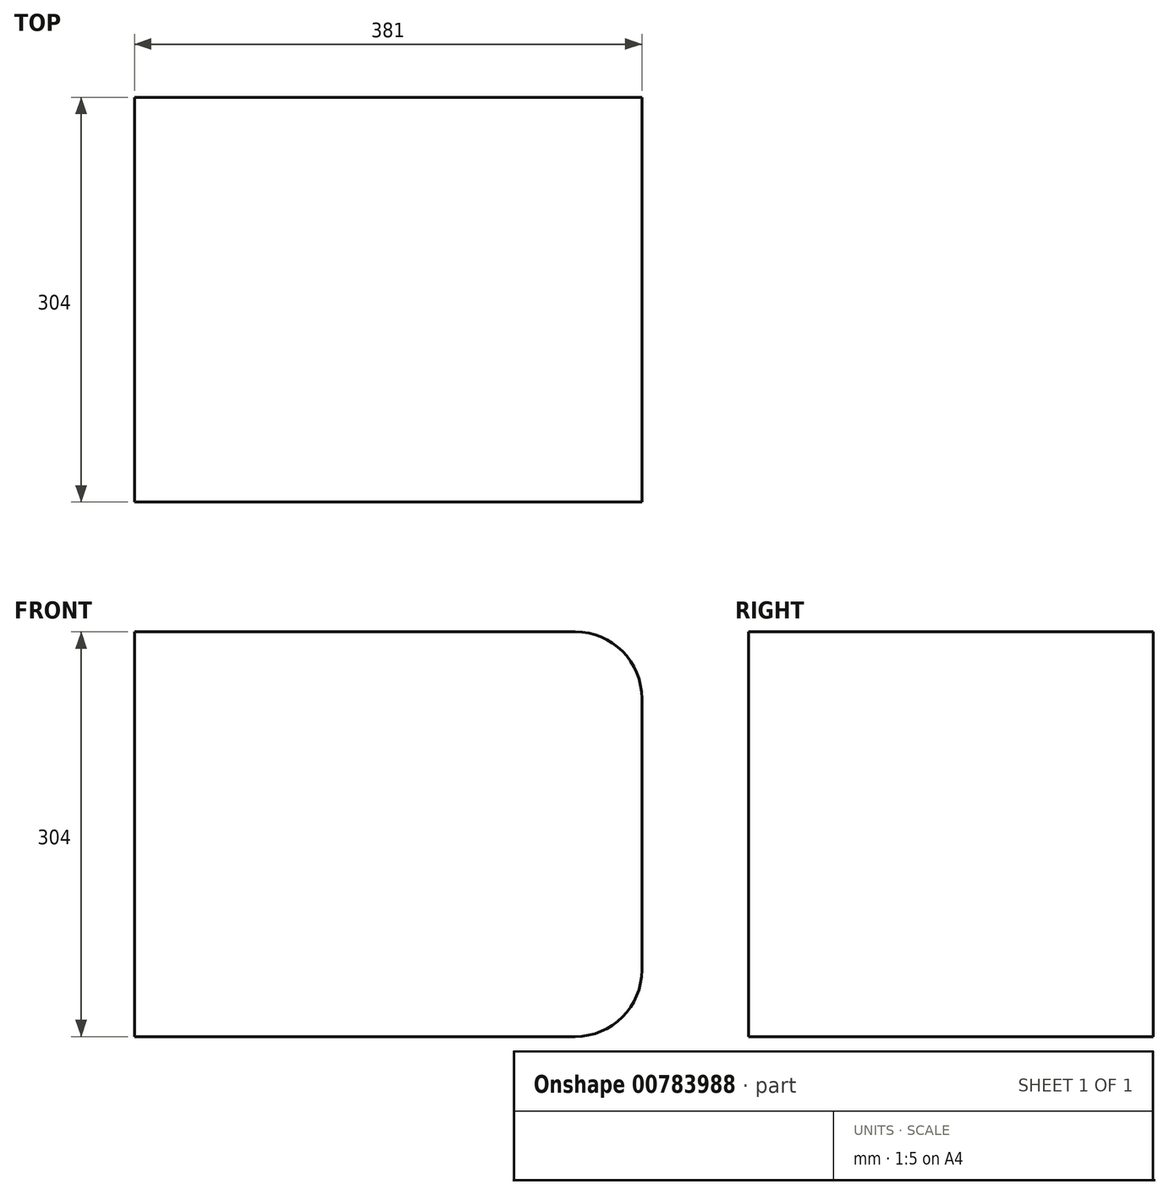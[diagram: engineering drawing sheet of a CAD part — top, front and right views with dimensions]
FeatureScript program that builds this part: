
annotation { "Feature Type Name" : "Feature", "Feature Type Description" : "" }
export const myFeature = defineFeature(function(context is Context, id is Id, definition is map)
    precondition{}
    {
        {
            var Q0;
            Q0=qCreatedBy(makeId("Front.planeOp"),FACE);
            var sketch = newSketch(context, id + "F0", { "sketchPlane" : qUnion([Q0])});
            skLineSegment(sketch, "E0.bottom", {"start": v(0, 0) * mm, "end": v(381, 0) * mm});
            skLineSegment(sketch, "E0.top", {"start": v(0, 304) * mm, "end": v(381, 304) * mm});
            skLineSegment(sketch, "E0.left", {"start": v(0, 0) * mm, "end": v(0, 304) * mm});
            skLineSegment(sketch, "E0.right", {"start": v(381, 0) * mm, "end": v(381, 304) * mm});
            skSolve(sketch);
        }
        {
            var Q0;
            Q0=makeQuery(id+"F0.imprint","IMPRINT",FACE,{"disambiguationData":[TD([[makeQuery(id+"F0.imprint","IMPRINT",EDGE,{"derivedFrom":sQuery(id+"F0.wireOp",EDGE,"E0.bottom")}),1.0]])]});
            extrude(context, id + "F1", {"entities" : qUnion([Q0]), "depth" : 304 * mm, "offsetDistance" : 25 * mm});
        }
        {
            var Q0;
            Q0=makeQuery(id+"F1.opExtrude","SWEPT_EDGE",EDGE,{"disambiguationData":[OSD([sQuery(id+"F0.wireOp",EDGE,"E0.top"),sQuery(id+"F0.wireOp",EDGE,"E0.right")])]});
            var Q1;
            Q1=makeQuery(id+"F1.opExtrude","SWEPT_EDGE",EDGE,{"disambiguationData":[OSD([sQuery(id+"F0.wireOp",EDGE,"E0.bottom"),sQuery(id+"F0.wireOp",EDGE,"E0.right")])]});
            fillet(context, id + "F2", {"entities" : qUnion([Q0, Q1]), "radius" : 50 * mm, "tangentPropagation" : true, "allowEdgeOverflow" : false});
        }
    });
